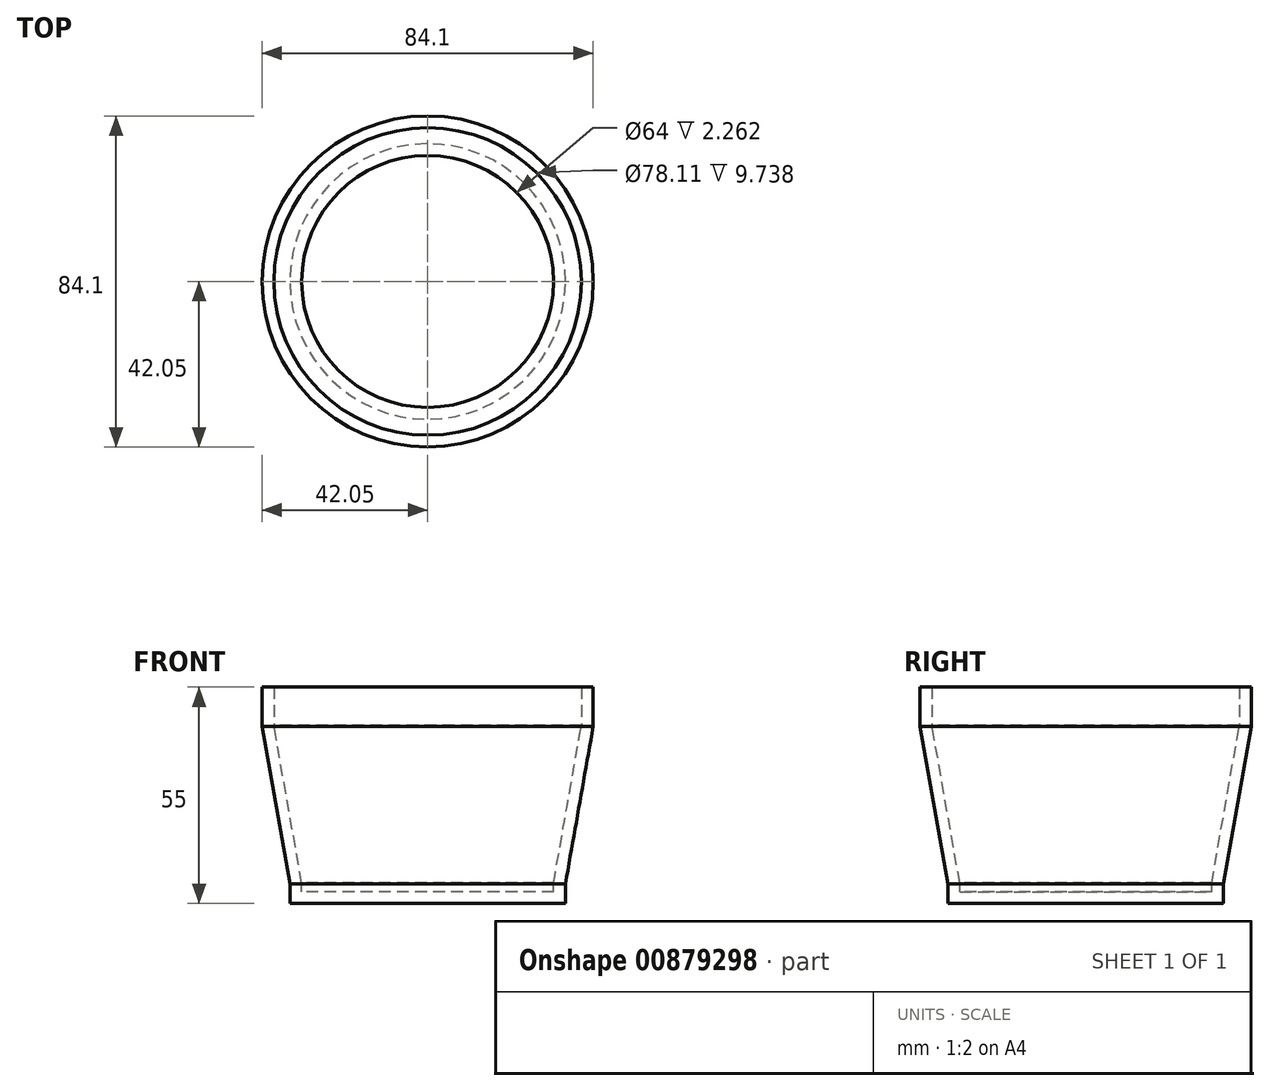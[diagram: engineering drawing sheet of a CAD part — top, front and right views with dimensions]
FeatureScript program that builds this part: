
annotation { "Feature Type Name" : "Feature", "Feature Type Description" : "" }
export const myFeature = defineFeature(function(context is Context, id is Id, definition is map)
    precondition{}
    {
        {
            var Q0;
            Q0=qCreatedBy(makeId("Top.planeOp"),FACE);
            var sketch = newSketch(context, id + "F0", { "sketchPlane" : qUnion([Q0])});
            skCircle(sketch, "E0", {"center": v(0, 0) * mm, "radius": 35 * mm});
            skSolve(sketch);
        }
        {
            var Q0;
            Q0 = qSketchRegion(id + "F0", true);
            extrude(context, id + "F1", {"entities" : qUnion([Q0]), "oppositeDirection" : true, "depth" : 5 * mm, "offsetDistance" : 25 * mm});
        }
        {
            var Q0;
            Q0=makeQuery(id+"F1.opExtrude","CAP_FACE",FACE,{"disambiguationData":[OSD([sQuery(id+"F0.wireOp",EDGE,"E0")])],"isStart":true});
            extrude(context, id + "F2", {"entities" : qUnion([Q0]), "operationType" : NewBodyOperationType.ADD, "depth" : 40 * mm, "offsetDistance" : 25 * mm, "hasDraft" : true, "draftAngle" : 10 * degree});
        }
        {
            var Q0;
            Q0=makeQuery(id+"F2.opExtrude","CAP_FACE",FACE,{"disambiguationData":[OSD([sQuery(id+"F0.wireOp",EDGE,"E0")])],"isStart":false});
            extrude(context, id + "F3", {"entities" : qUnion([Q0]), "operationType" : NewBodyOperationType.ADD, "depth" : 10 * mm, "offsetDistance" : 25 * mm});
        }
        {
            var Q0;
            Q0=makeQuery(id+"F3.opExtrude","CAP_FACE",FACE,{"disambiguationData":[OSD([sQuery(id+"F0.wireOp",EDGE,"E0")])],"isStart":false});
            shell(context, id + "F4", {"entities" : qUnion([Q0]), "thickness" : 3 * mm});
        }
    });
